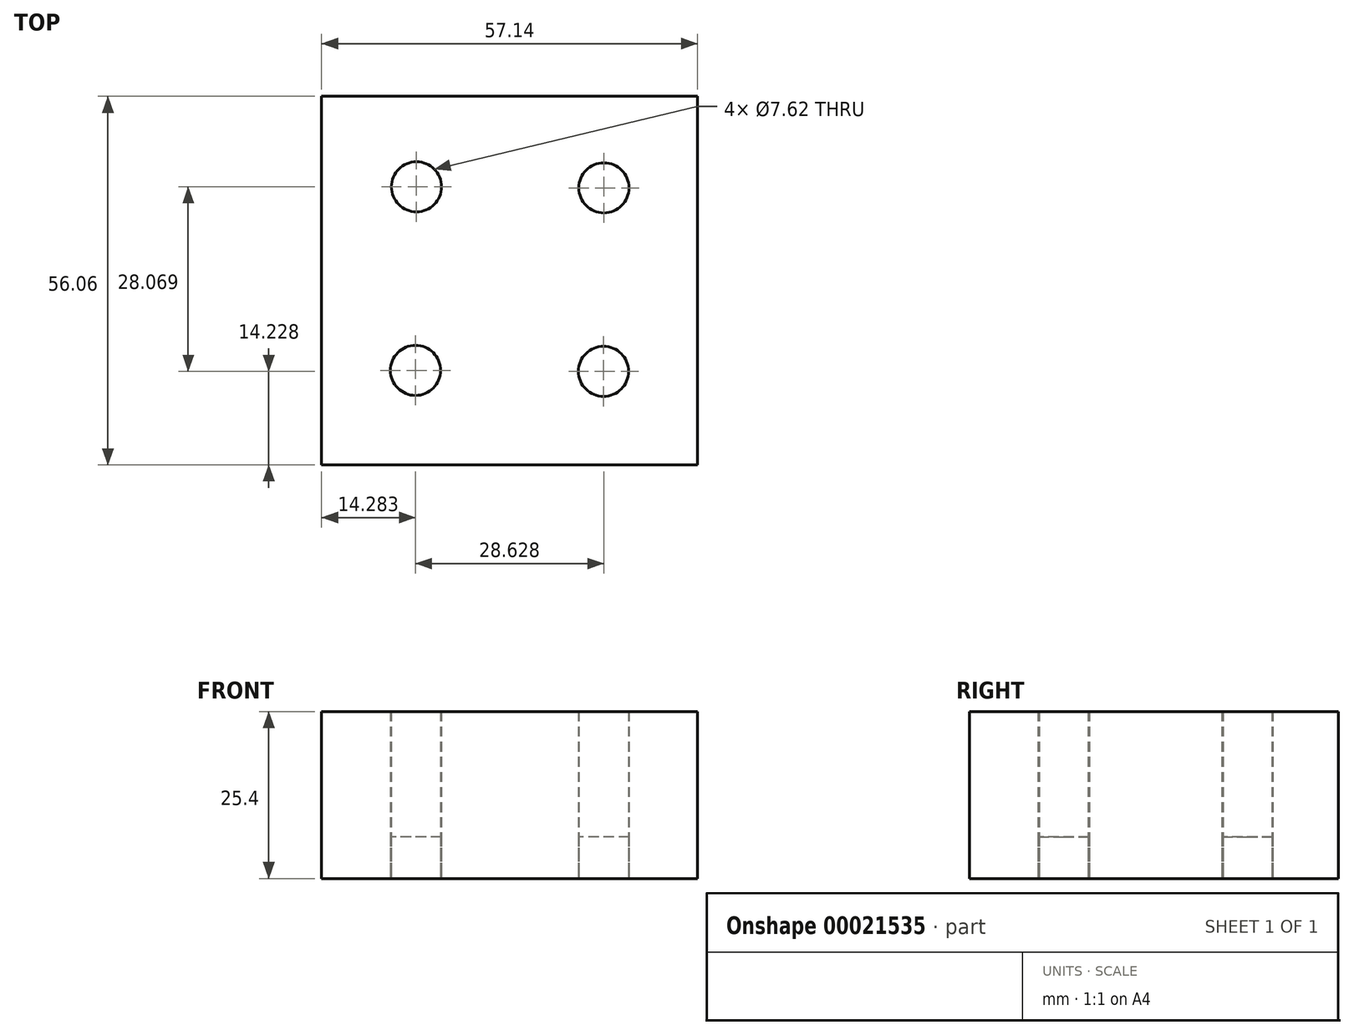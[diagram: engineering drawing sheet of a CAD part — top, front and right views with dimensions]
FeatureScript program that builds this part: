
annotation { "Feature Type Name" : "Feature", "Feature Type Description" : "" }
export const myFeature = defineFeature(function(context is Context, id is Id, definition is map)
    precondition{}
    {
        {
            var Q0;
            Q0=qCreatedBy(makeId("Top.planeOp"),FACE);
            var sketch = newSketch(context, id + "F0", { "sketchPlane" : qUnion([Q0])});
            skPoint(sketch, "E0.start.orphan", {"position": v(0, -57.48) * mm});
            skPoint(sketch, "E1.start.orphan", {"position": v(138.1, 0) * mm});
            skLineSegment(sketch, "E2", {"start": v(0, 27.32) * mm, "end": v(28.58, 27.32) * mm});
            skLineSegment(sketch, "E3", {"start": v(28.58, 27.32) * mm, "end": v(28.58, -28.74) * mm});
            skLineSegment(sketch, "E4", {"start": v(28.58, 27.32) * mm, "end": v(-28.57, 27.32) * mm});
            skLineSegment(sketch, "E5", {"start": v(28.58, -28.74) * mm, "end": v(0, -28.74) * mm});
            skLineSegment(sketch, "E6", {"start": v(0, 27.32) * mm, "end": v(-28.57, 27.32) * mm});
            skLineSegment(sketch, "E7", {"start": v(-28.57, 27.32) * mm, "end": v(-28.57, 0) * mm});
            skPoint(sketch, "E8.orphan", {"position": v(-57.15, 56.82) * mm});
            skPoint(sketch, "E9.orphan", {"position": v(-57.15, 27.32) * mm});
            skPoint(sketch, "E10.orphan", {"position": v(57.15, 56.82) * mm});
            skPoint(sketch, "E11.orphan", {"position": v(57.15, 27.32) * mm});
            skPoint(sketch, "E12.start.orphan", {"position": v(57.15, -28.74) * mm});
            skPoint(sketch, "E13.orphan", {"position": v(57.15, -57.48) * mm});
            skPoint(sketch, "E14.orphan", {"position": v(57.15, 0) * mm});
            skPoint(sketch, "E15.orphan", {"position": v(0, 56.82) * mm});
            skPoint(sketch, "E16.start.orphan", {"position": v(-57.15, -57.48) * mm});
            skLineSegment(sketch, "E17", {"start": v(0, -28.74) * mm, "end": v(-28.57, -28.74) * mm});
            skPoint(sketch, "E18.end.orphan", {"position": v(-28.57, -27.32) * mm});
            skLineSegment(sketch, "E19", {"start": v(-28.57, 0) * mm, "end": v(-28.57, -28.74) * mm});
            skPoint(sketch, "E20.orphan", {"position": v(-28.57, -14.37) * mm});
            skPoint(sketch, "E21.orphan", {"position": v(-14.29, -28.74) * mm});
            skCircle(sketch, "E22", {"center": v(-14.29, -14.37) * mm, "radius": 3.81 * mm});
            skCircle(sketch, "E23", {"center": v(14.29, -14.51) * mm, "radius": 3.81 * mm});
            skCircle(sketch, "E24", {"center": v(14.34, 13.4) * mm, "radius": 3.81 * mm});
            skCircle(sketch, "E25", {"center": v(-14.14, 13.56) * mm, "radius": 3.81 * mm});
            skPoint(sketch, "E26.orphan", {"position": v(-14.29, 27.32) * mm});
            skPoint(sketch, "E27.orphan", {"position": v(-28.57, 13.66) * mm});
            skPoint(sketch, "E28.orphan", {"position": v(14.29, 27.32) * mm});
            skPoint(sketch, "E29.orphan", {"position": v(14.29, -28.74) * mm});
            skPoint(sketch, "E30.orphan", {"position": v(-57.15, 0) * mm});
            skSolve(sketch);
        }
        {
            var Q0;
            Q0=makeQuery(id+"F0.imprint","IMPRINT",FACE,{"disambiguationData":[TD([[makeQuery(id+"F0.imprint","IMPRINT",EDGE,{"derivedFrom":sQuery(id+"F0.wireOp",EDGE,"E3")}),-1.0]])]});
            extrude(context, id + "F1", {"entities" : qUnion([Q0]), "depth" : 25.4 * mm});
        }
        {
            var Q0;
            Q0=makeQuery(id+"F0.imprint","IMPRINT",FACE,{"disambiguationData":[TD([[makeQuery(id+"F0.imprint","IMPRINT",EDGE,{"derivedFrom":sQuery(id+"F0.wireOp",EDGE,"E25")}),1.0]])]});
            var Q1;
            Q1=makeQuery(id+"F0.imprint","IMPRINT",FACE,{"disambiguationData":[TD([[makeQuery(id+"F0.imprint","IMPRINT",EDGE,{"derivedFrom":sQuery(id+"F0.wireOp",EDGE,"E22")}),1.0]])]});
            var Q2;
            Q2=makeQuery(id+"F0.imprint","IMPRINT",FACE,{"disambiguationData":[TD([[makeQuery(id+"F0.imprint","IMPRINT",EDGE,{"derivedFrom":sQuery(id+"F0.wireOp",EDGE,"E23")}),1.0]])]});
            var Q3;
            Q3=makeQuery(id+"F0.imprint","IMPRINT",FACE,{"disambiguationData":[TD([[makeQuery(id+"F0.imprint","IMPRINT",EDGE,{"derivedFrom":sQuery(id+"F0.wireOp",EDGE,"E24")}),1.0]])]});
            extrude(context, id + "F2", {"entities" : qUnion([Q0, Q1, Q2, Q3]), "depth" : 6.35 * mm});
        }
    });
